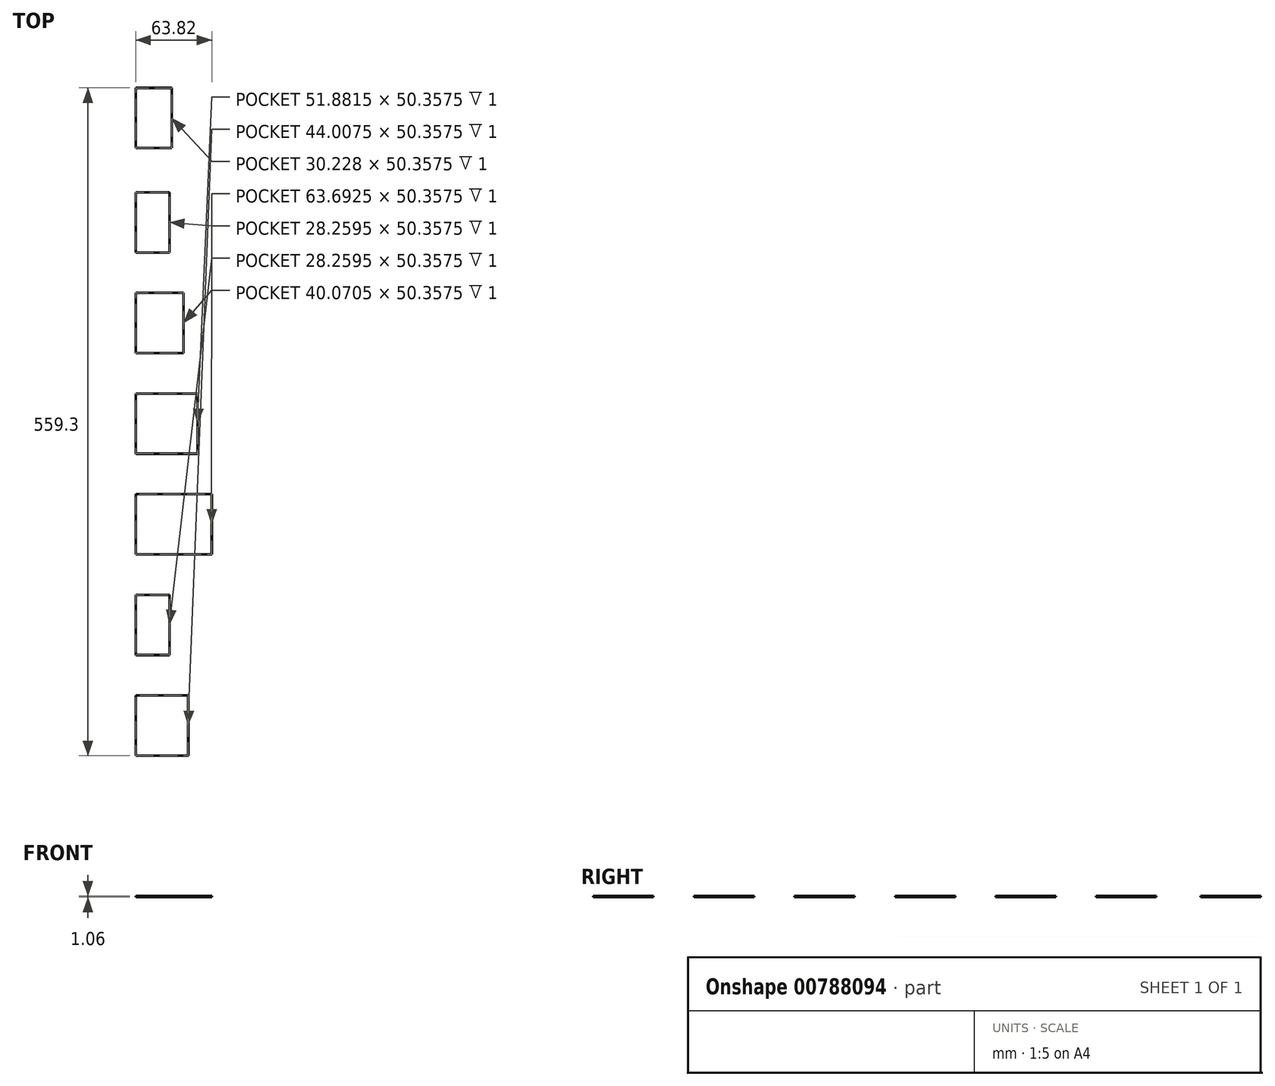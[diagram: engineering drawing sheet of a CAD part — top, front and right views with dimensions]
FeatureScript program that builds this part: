
annotation { "Feature Type Name" : "Feature", "Feature Type Description" : "" }
export const myFeature = defineFeature(function(context is Context, id is Id, definition is map)
    precondition{}
    {
        {
            assignVariable(context, id + "F0", {"name" : "wallthick", "anyValue" : 1 / 16});
        }
        {
            assignVariable(context, id + "F1", {"name" : "holderdepth", "anyValue" : 1});
        }
        {
            var Q0;
            Q0=qCreatedBy(makeId("Top.planeOp"),FACE);
            var sketch = newSketch(context, id + "F2", { "sketchPlane" : qUnion([Q0])});
            skLineSegment(sketch, "E0.bottom", {"start": v(0, 0) * mm, "end": v(25.2, 0) * mm});
            skLineSegment(sketch, "E0.top", {"start": v(0, -47.3) * mm, "end": v(25.2, -47.3) * mm});
            skLineSegment(sketch, "E0.left", {"start": v(0, 0) * mm, "end": v(0, -47.3) * mm});
            skLineSegment(sketch, "E0.right", {"start": v(25.2, 0) * mm, "end": v(25.2, -47.3) * mm});
            skLineSegment(sketch, "E1.bottom", {"start": v(0, -84.27) * mm, "end": v(37.02, -84.27) * mm});
            skLineSegment(sketch, "E1.top", {"start": v(0, -131.58) * mm, "end": v(37.02, -131.58) * mm});
            skLineSegment(sketch, "E1.left", {"start": v(0, -84.27) * mm, "end": v(0, -131.58) * mm});
            skLineSegment(sketch, "E1.right", {"start": v(37.02, -84.27) * mm, "end": v(37.02, -131.58) * mm});
            skLineSegment(sketch, "E2.bottom", {"start": v(0, 40.14) * mm, "end": v(27.18, 40.14) * mm});
            skLineSegment(sketch, "E2.top", {"start": v(0, 87.45) * mm, "end": v(27.18, 87.45) * mm});
            skLineSegment(sketch, "E2.left", {"start": v(0, 40.14) * mm, "end": v(0, 87.45) * mm});
            skLineSegment(sketch, "E2.right", {"start": v(27.18, 40.14) * mm, "end": v(27.18, 87.45) * mm});
            skLineSegment(sketch, "E3", {"start": v(0, -84.27) * mm, "end": v(0, -47.3) * mm, "construction": true});
            skLineSegment(sketch, "E4", {"start": v(0, 0) * mm, "end": v(0, 40.14) * mm, "construction": true});
            skLineSegment(sketch, "E5.bottom", {"start": v(0, -168.55) * mm, "end": v(48.83, -168.55) * mm});
            skLineSegment(sketch, "E5.top", {"start": v(0, -215.85) * mm, "end": v(48.83, -215.85) * mm});
            skLineSegment(sketch, "E5.left", {"start": v(0, -168.55) * mm, "end": v(0, -215.85) * mm});
            skLineSegment(sketch, "E5.right", {"start": v(48.83, -168.55) * mm, "end": v(48.83, -215.85) * mm});
            skLineSegment(sketch, "E6.bottom", {"start": v(0, -252.82) * mm, "end": v(60.64, -252.82) * mm});
            skLineSegment(sketch, "E6.top", {"start": v(0, -300.13) * mm, "end": v(60.64, -300.13) * mm});
            skLineSegment(sketch, "E6.left", {"start": v(0, -252.82) * mm, "end": v(0, -300.13) * mm});
            skLineSegment(sketch, "E6.right", {"start": v(60.64, -252.82) * mm, "end": v(60.64, -300.13) * mm});
            skLineSegment(sketch, "E7.bottom", {"start": v(0, -337.1) * mm, "end": v(25.2, -337.1) * mm});
            skLineSegment(sketch, "E7.top", {"start": v(0, -384.4) * mm, "end": v(25.2, -384.4) * mm});
            skLineSegment(sketch, "E7.left", {"start": v(0, -337.1) * mm, "end": v(0, -384.4) * mm});
            skLineSegment(sketch, "E7.right", {"start": v(25.2, -337.1) * mm, "end": v(25.2, -384.4) * mm});
            skLineSegment(sketch, "E8.bottom", {"start": v(0, -421.36) * mm, "end": v(40.96, -421.36) * mm});
            skLineSegment(sketch, "E8.top", {"start": v(0, -468.67) * mm, "end": v(40.96, -468.67) * mm});
            skLineSegment(sketch, "E8.left", {"start": v(0, -421.36) * mm, "end": v(0, -468.67) * mm});
            skLineSegment(sketch, "E8.right", {"start": v(40.96, -421.36) * mm, "end": v(40.96, -468.67) * mm});
            skLineSegment(sketch, "E9", {"start": v(0, -421.36) * mm, "end": v(0, -384.4) * mm, "construction": true});
            skLineSegment(sketch, "E10", {"start": v(0, -337.1) * mm, "end": v(0, -300.13) * mm, "construction": true});
            skLineSegment(sketch, "E11", {"start": v(0, -252.82) * mm, "end": v(0, -215.85) * mm, "construction": true});
            skLineSegment(sketch, "E12", {"start": v(0, -168.55) * mm, "end": v(0, -131.58) * mm, "construction": true});
            skSolve(sketch);
        }
        {
            var Q0;
            Q0=qCreatedBy(makeId("Top.planeOp"),FACE);
            var sketch = newSketch(context, id + "F3", { "sketchPlane" : qUnion([Q0])});
            skLineSegment(sketch, "E13.0", {"start": v(28.77, 89.04) * mm, "end": v(-1.59, 89.04) * mm});
            skLineSegment(sketch, "E13.1", {"start": v(28.77, 38.55) * mm, "end": v(28.77, 89.04) * mm});
            skLineSegment(sketch, "E13.2", {"start": v(-1.59, 38.55) * mm, "end": v(28.77, 38.55) * mm});
            skLineSegment(sketch, "E13.3", {"start": v(-1.59, 89.04) * mm, "end": v(-1.59, 38.55) * mm});
            skLineSegment(sketch, "E14.0", {"start": v(-1.59, 1.59) * mm, "end": v(-1.59, -48.9) * mm});
            skLineSegment(sketch, "E14.1", {"start": v(26.8, 1.59) * mm, "end": v(-1.59, 1.59) * mm});
            skLineSegment(sketch, "E14.2", {"start": v(26.8, -48.9) * mm, "end": v(26.8, 1.59) * mm});
            skLineSegment(sketch, "E14.3", {"start": v(-1.59, -48.9) * mm, "end": v(26.8, -48.9) * mm});
            skLineSegment(sketch, "E15.0", {"start": v(-1.59, -82.69) * mm, "end": v(-1.59, -133.17) * mm});
            skLineSegment(sketch, "E15.1", {"start": v(38.6, -82.69) * mm, "end": v(-1.59, -82.69) * mm});
            skLineSegment(sketch, "E15.2", {"start": v(38.6, -133.17) * mm, "end": v(38.6, -82.69) * mm});
            skLineSegment(sketch, "E15.3", {"start": v(-1.59, -133.17) * mm, "end": v(38.6, -133.17) * mm});
            skLineSegment(sketch, "E16.0", {"start": v(-1.59, -166.96) * mm, "end": v(-1.59, -217.44) * mm});
            skLineSegment(sketch, "E16.1", {"start": v(50.42, -166.96) * mm, "end": v(-1.59, -166.96) * mm});
            skLineSegment(sketch, "E16.2", {"start": v(50.42, -217.44) * mm, "end": v(50.42, -166.96) * mm});
            skLineSegment(sketch, "E16.3", {"start": v(-1.59, -217.44) * mm, "end": v(50.42, -217.44) * mm});
            skLineSegment(sketch, "E17.0", {"start": v(-1.59, -251.23) * mm, "end": v(-1.59, -301.71) * mm});
            skLineSegment(sketch, "E17.1", {"start": v(62.23, -251.23) * mm, "end": v(-1.59, -251.23) * mm});
            skLineSegment(sketch, "E17.2", {"start": v(62.23, -301.71) * mm, "end": v(62.23, -251.23) * mm});
            skLineSegment(sketch, "E17.3", {"start": v(-1.59, -301.71) * mm, "end": v(62.23, -301.71) * mm});
            skLineSegment(sketch, "E18.0", {"start": v(-1.59, -335.5) * mm, "end": v(-1.59, -385.99) * mm});
            skLineSegment(sketch, "E18.1", {"start": v(26.8, -335.5) * mm, "end": v(-1.59, -335.5) * mm});
            skLineSegment(sketch, "E18.2", {"start": v(26.8, -385.99) * mm, "end": v(26.8, -335.5) * mm});
            skLineSegment(sketch, "E18.3", {"start": v(-1.59, -385.99) * mm, "end": v(26.8, -385.99) * mm});
            skLineSegment(sketch, "E19.0", {"start": v(-1.59, -419.78) * mm, "end": v(-1.59, -470.26) * mm});
            skLineSegment(sketch, "E19.1", {"start": v(42.55, -419.78) * mm, "end": v(-1.59, -419.78) * mm});
            skLineSegment(sketch, "E19.2", {"start": v(42.55, -470.26) * mm, "end": v(42.55, -419.78) * mm});
            skLineSegment(sketch, "E19.3", {"start": v(-1.59, -470.26) * mm, "end": v(42.55, -470.26) * mm});
            skSolve(sketch);
        }
        {
            var Q0;
            Q0 = qSketchRegion(id + "F3", true);
            extrude(context, id + "F4", {"entities" : qUnion([Q0]), "depth" : (getVariable(context, 'holderdepth') + getVariable(context, 'wallthick')) * mm, "offsetDistance" : 25.4 * mm});
        }
        {
            var Q0;
            Q0=makeQuery(id+"F4.opExtrude","CAP_FACE",FACE,{"disambiguationData":[OSD([sQuery(id+"F3.wireOp",EDGE,"577c2206-77e0-4c73-9001-d3933ba6cb78.0"),sQuery(id+"F3.wireOp",EDGE,"577c2206-77e0-4c73-9001-d3933ba6cb78.1"),sQuery(id+"F3.wireOp",EDGE,"577c2206-77e0-4c73-9001-d3933ba6cb78.2"),sQuery(id+"F3.wireOp",EDGE,"577c2206-77e0-4c73-9001-d3933ba6cb78.3")])],"isStart":false});
            var Q1;
            Q1=makeQuery(id+"F4.opExtrude","CAP_FACE",FACE,{"disambiguationData":[OSD([sQuery(id+"F3.wireOp",EDGE,"E19.0"),sQuery(id+"F3.wireOp",EDGE,"E19.1"),sQuery(id+"F3.wireOp",EDGE,"E19.2"),sQuery(id+"F3.wireOp",EDGE,"E19.3")])],"isStart":false});
            var Q2;
            Q2=makeQuery(id+"F4.opExtrude","CAP_FACE",FACE,{"disambiguationData":[OSD([sQuery(id+"F3.wireOp",EDGE,"E18.0"),sQuery(id+"F3.wireOp",EDGE,"E18.1"),sQuery(id+"F3.wireOp",EDGE,"E18.2"),sQuery(id+"F3.wireOp",EDGE,"E18.3")])],"isStart":false});
            var Q3;
            Q3=makeQuery(id+"F4.opExtrude","CAP_FACE",FACE,{"disambiguationData":[OSD([sQuery(id+"F3.wireOp",EDGE,"E17.0"),sQuery(id+"F3.wireOp",EDGE,"E17.1"),sQuery(id+"F3.wireOp",EDGE,"E17.2"),sQuery(id+"F3.wireOp",EDGE,"E17.3")])],"isStart":false});
            var Q4;
            Q4=makeQuery(id+"F4.opExtrude","CAP_FACE",FACE,{"disambiguationData":[OSD([sQuery(id+"F3.wireOp",EDGE,"E16.0"),sQuery(id+"F3.wireOp",EDGE,"E16.1"),sQuery(id+"F3.wireOp",EDGE,"E16.2"),sQuery(id+"F3.wireOp",EDGE,"E16.3")])],"isStart":false});
            var Q5;
            Q5=makeQuery(id+"F4.opExtrude","CAP_FACE",FACE,{"disambiguationData":[OSD([sQuery(id+"F3.wireOp",EDGE,"E15.0"),sQuery(id+"F3.wireOp",EDGE,"E15.1"),sQuery(id+"F3.wireOp",EDGE,"E15.2"),sQuery(id+"F3.wireOp",EDGE,"E15.3")])],"isStart":false});
            var Q6;
            Q6=makeQuery(id+"F4.opExtrude","CAP_FACE",FACE,{"disambiguationData":[OSD([sQuery(id+"F3.wireOp",EDGE,"E14.0"),sQuery(id+"F3.wireOp",EDGE,"E14.1"),sQuery(id+"F3.wireOp",EDGE,"E14.2"),sQuery(id+"F3.wireOp",EDGE,"E14.3")])],"isStart":false});
            var Q7;
            Q7=makeQuery(id+"F4.opExtrude","CAP_FACE",FACE,{"disambiguationData":[OSD([sQuery(id+"F3.wireOp",EDGE,"E13.0"),sQuery(id+"F3.wireOp",EDGE,"E13.1"),sQuery(id+"F3.wireOp",EDGE,"E13.2"),sQuery(id+"F3.wireOp",EDGE,"E13.3")])],"isStart":false});
            var Q8;
            Q8=makeQuery(id+"F4.opExtrude","CAP_FACE",FACE,{"disambiguationData":[OSD([sQuery(id+"F3.wireOp",EDGE,"833aac4a-94a2-4c84-8c4b-cff8638e51e8.0"),sQuery(id+"F3.wireOp",EDGE,"833aac4a-94a2-4c84-8c4b-cff8638e51e8.1"),sQuery(id+"F3.wireOp",EDGE,"833aac4a-94a2-4c84-8c4b-cff8638e51e8.2"),sQuery(id+"F3.wireOp",EDGE,"833aac4a-94a2-4c84-8c4b-cff8638e51e8.3")])],"isStart":false});
            shell(context, id + "F5", {"entities" : qUnion([Q0, Q1, Q2, Q3, Q4, Q5, Q6, Q7, Q8]), "thickness" : (getVariable(context, 'wallthick')) * mm});
        }
    });
